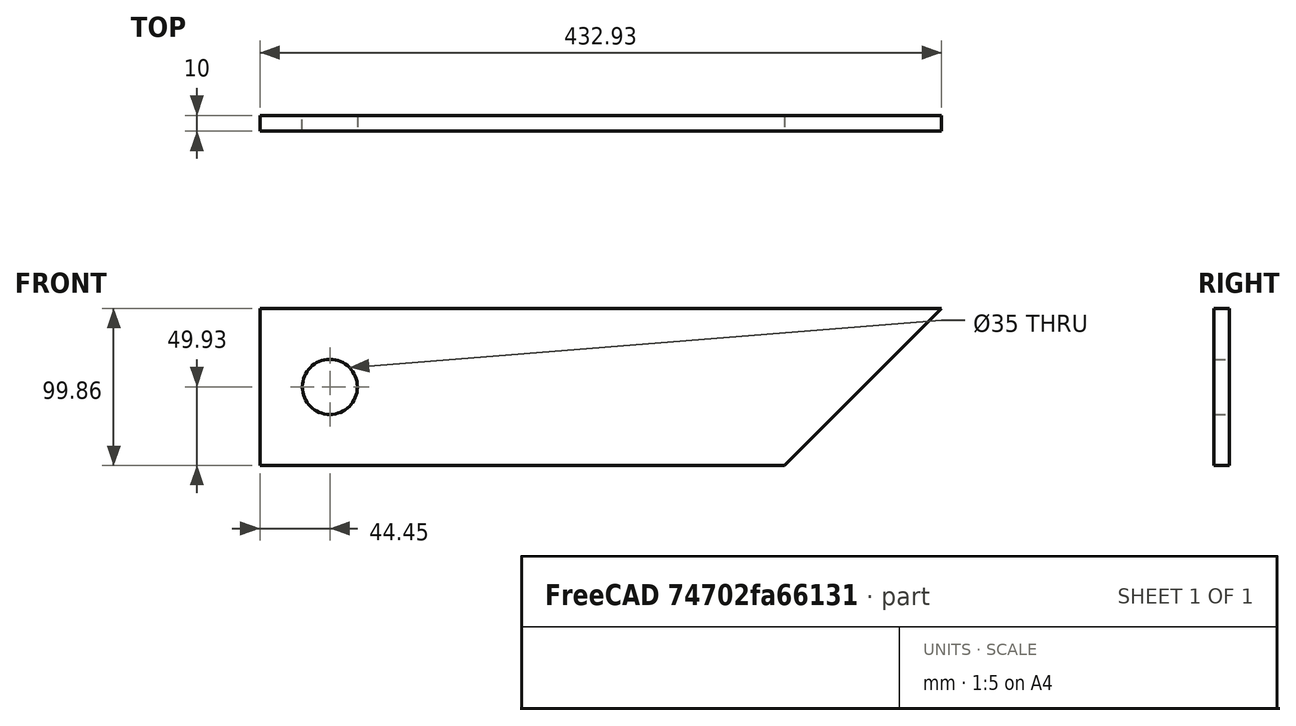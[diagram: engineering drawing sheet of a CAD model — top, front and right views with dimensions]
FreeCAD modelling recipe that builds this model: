
FCSTD DOCUMENT  (FreeCAD 0.21R33771 (Git))
Label: YawBearing_Extended_Top
License: All rights reserved
LicenseURL: http://en.wikipedia.org/wiki/All_rights_reserved
objects: Sketcher::SketchObject×1, PartDesign::Pad×1, PartDesign::Body×1, Spreadsheet::Sheet×1
note: 4 computed .brp shape members not serialized (recipe doc carries the construction recipe); baked Part::Feature solids carry a one-line shape summary decoded from their .brp
EXTERNAL_REF file=../../Master_of_Puppets.FCStd obj=Spreadsheet
EXTERNAL_REF file=../../Master_of_Puppets.FCStd obj=YawBearing

FEATURE [Sketcher::SketchObject] Sketch
  FullyConstrained = true
  MapMode = 5
  Placement = pos=(0,0,0) rot=(1,0,0;1.5708rad)
  Support = -> [XZ_Plane]
  expr: Constraints[0] = Spreadsheet.YawPipeRadius
  expr: Constraints[11] = Spreadsheet.L
  expr: Constraints[12] = Spreadsheet.TopAngle
  expr: Constraints[13] = Spreadsheet.Width / 2
  expr: Constraints[14] = Spreadsheet.Width
  expr: Constraints[15] = Spreadsheet.YawPipeRadius
  expr: Constraints[2] = Spreadsheet.YawBearingPlateTopHoleRadius
  sketch-geometry (6):
    g0: Circle CenterX=44.45 CenterY=49.9296 CenterZ=0 NormalX=0 NormalY=0 NormalZ=1 AngleXU=0 Radius=44.45
    g1: LineSegment StartX=333.067 StartY=0 StartZ=0 EndX=432.927 EndY=99.8592 EndZ=0
    g2: Circle CenterX=44.45 CenterY=49.9296 CenterZ=0 NormalX=0 NormalY=0 NormalZ=1 AngleXU=0 Radius=17.5
    g3: LineSegment StartX=0 StartY=0 StartZ=0 EndX=333.067 EndY=0 EndZ=0
    g4: LineSegment StartX=432.927 StartY=99.8592 StartZ=0 EndX=0 EndY=99.8592 EndZ=0
    g5: LineSegment StartX=0 StartY=0 StartZ=0 EndX=0 EndY=99.8592 EndZ=0
  constraints (16):
    c: Radius(g0) = 44.45
    c: Coincident(g2,g0)
    c: Radius(g2) = 17.5
    c: Coincident(g3,g-1)
    c: Coincident(g3,g1)
    c: Horizontal(g3)
    c: Coincident(g4,g1)
    c: Horizontal(g4)
    c: Coincident(g5,g3)
    c: Coincident(g5,g4)
    c: Vertical(g5)
    c: DistanceX(g4,g1) = 432.927
    c: Angle(g4,g1) = 0.785398
    c: DistanceY(g3,g2) = 49.9296
    c: DistanceY(g4) = 99.8592
    c: DistanceX(g-2,g2) = 44.45
FEATURE [PartDesign::Pad] Pad
  AllowMultiFace = false
  Direction = (0,-1,-1.035e-13)
  Length = 10
  Length2 = 100
  Placement = pos=(0,0,0) rot=(1,0,0;1.5708rad)
  Profile = -> Sketch
  Type = 0
  expr: Length = Spreadsheet.FlatMetalThickness
FEATURE [PartDesign::Body] Body  label="YawBearing_Extended_Top"
  Group = -> [Sketch,Pad]
  Openafpm_Flat = true
  Origin = -> Origin
  Tip = -> Pad
FEATURE [Spreadsheet::Sheet] Spreadsheet
  cells = A1='Inputs; A2='RotorDiskRadius; B2(RotorDiskRadius)==Master_of_Puppets#Spreadsheet.RotorDiskRadius; A3='YawPipeDiameter; B3(YawPipeDiameter)==Master_of_Puppets#Spreadsheet.YawPipeDiameter; A4='FlatMetalThickness; B4(FlatMetalThickness)==Master_of_Puppets#Spreadsheet.FlatMetalThickness; A5='Width; B5(Width)==Master_of_Puppets#YawBearing.MM; A6='Offset; B6(Offset)==Master_of_Puppets#Spreadsheet.Offset; A7='YawBearingPlateTopHoleRadius; B7(YawBearingPlateTopHoleRadius)==Master_of_Puppets#YawBearing.YawBearingPlateTopHoleRadius; A8='TopAngle; B8(TopAngle)==Master_of_Puppets#YawBearing.TopAngle; A9='L; B9(L)==Master_of_Puppets#YawBearing.L; A10='Calculated; A11='YawPipeRadius; B11(YawPipeRadius)==YawPipeDiameter / 2
